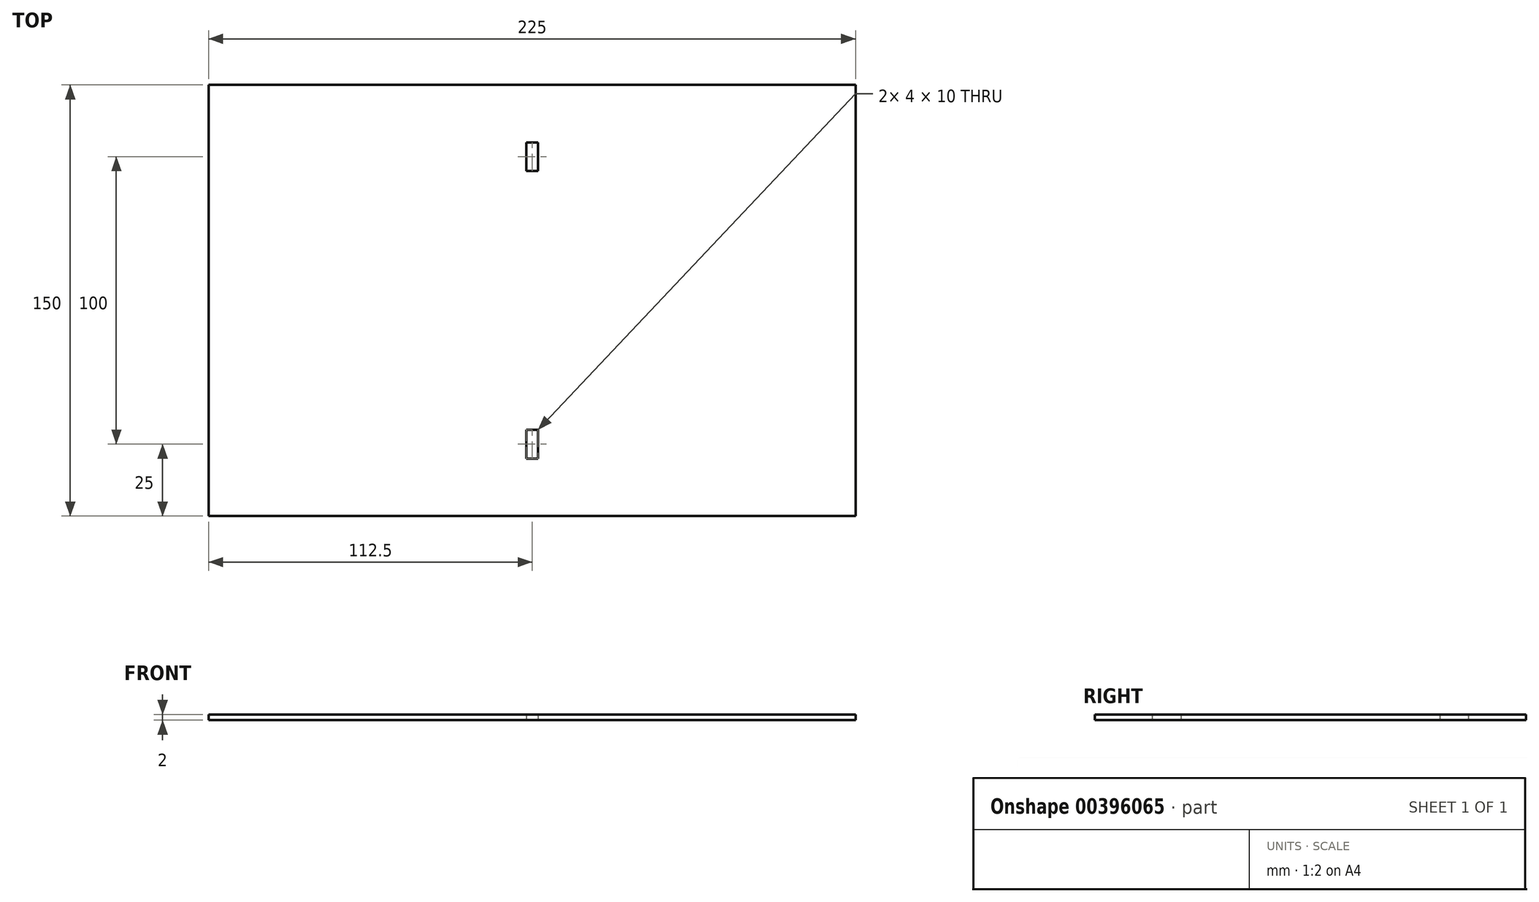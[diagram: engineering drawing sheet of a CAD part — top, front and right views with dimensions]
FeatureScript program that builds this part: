
annotation { "Feature Type Name" : "Feature", "Feature Type Description" : "" }
export const myFeature = defineFeature(function(context is Context, id is Id, definition is map)
    precondition{}
    {
        {
            var Q0;
            Q0=qCreatedBy(makeId("Top.planeOp"),FACE);
            var sketch = newSketch(context, id + "F0", { "sketchPlane" : qUnion([Q0])});
            skLineSegment(sketch, "E0", {"start": v(-63.93, 0) * mm, "end": v(86.07, 0) * mm, "construction": true});
            skLineSegment(sketch, "E1", {"start": v(0, -54.58) * mm, "end": v(0, 95.42) * mm, "construction": true});
            skLineSegment(sketch, "E2.bottom", {"start": v(-2, 55) * mm, "end": v(2, 55) * mm});
            skLineSegment(sketch, "E2.top", {"start": v(-2, 45) * mm, "end": v(2, 45) * mm});
            skLineSegment(sketch, "E2.left", {"start": v(-2, 55) * mm, "end": v(-2, 45) * mm});
            skLineSegment(sketch, "E2.right", {"start": v(2, 55) * mm, "end": v(2, 45) * mm});
            skPoint(sketch, "E2.middle", {"position": v(0, 50) * mm});
            skLineSegment(sketch, "E3.MirrorCS", {"start": v(-2, -55) * mm, "end": v(-2, -45) * mm});
            skLineSegment(sketch, "E4.MirrorCS", {"start": v(-2, -55) * mm, "end": v(2, -55) * mm});
            skLineSegment(sketch, "E5.MirrorCS", {"start": v(2, -55) * mm, "end": v(2, -45) * mm});
            skLineSegment(sketch, "E6.MirrorCS", {"start": v(-2, -45) * mm, "end": v(2, -45) * mm});
            skLineSegment(sketch, "E7.bottom", {"start": v(-112.5, 75) * mm, "end": v(112.5, 75) * mm});
            skLineSegment(sketch, "E7.top", {"start": v(-112.5, -75) * mm, "end": v(112.5, -75) * mm});
            skLineSegment(sketch, "E7.left", {"start": v(-112.5, 75) * mm, "end": v(-112.5, -75) * mm});
            skLineSegment(sketch, "E7.right", {"start": v(112.5, 75) * mm, "end": v(112.5, -75) * mm});
            skPoint(sketch, "E7.middle", {"position": v(0, 0) * mm});
            skSolve(sketch);
        }
        {
            var Q0;
            Q0 = qSketchRegion(id + "F0", true);
            extrude(context, id + "F1", {"entities" : qUnion([Q0]), "depth" : 2 * mm});
        }
    });
